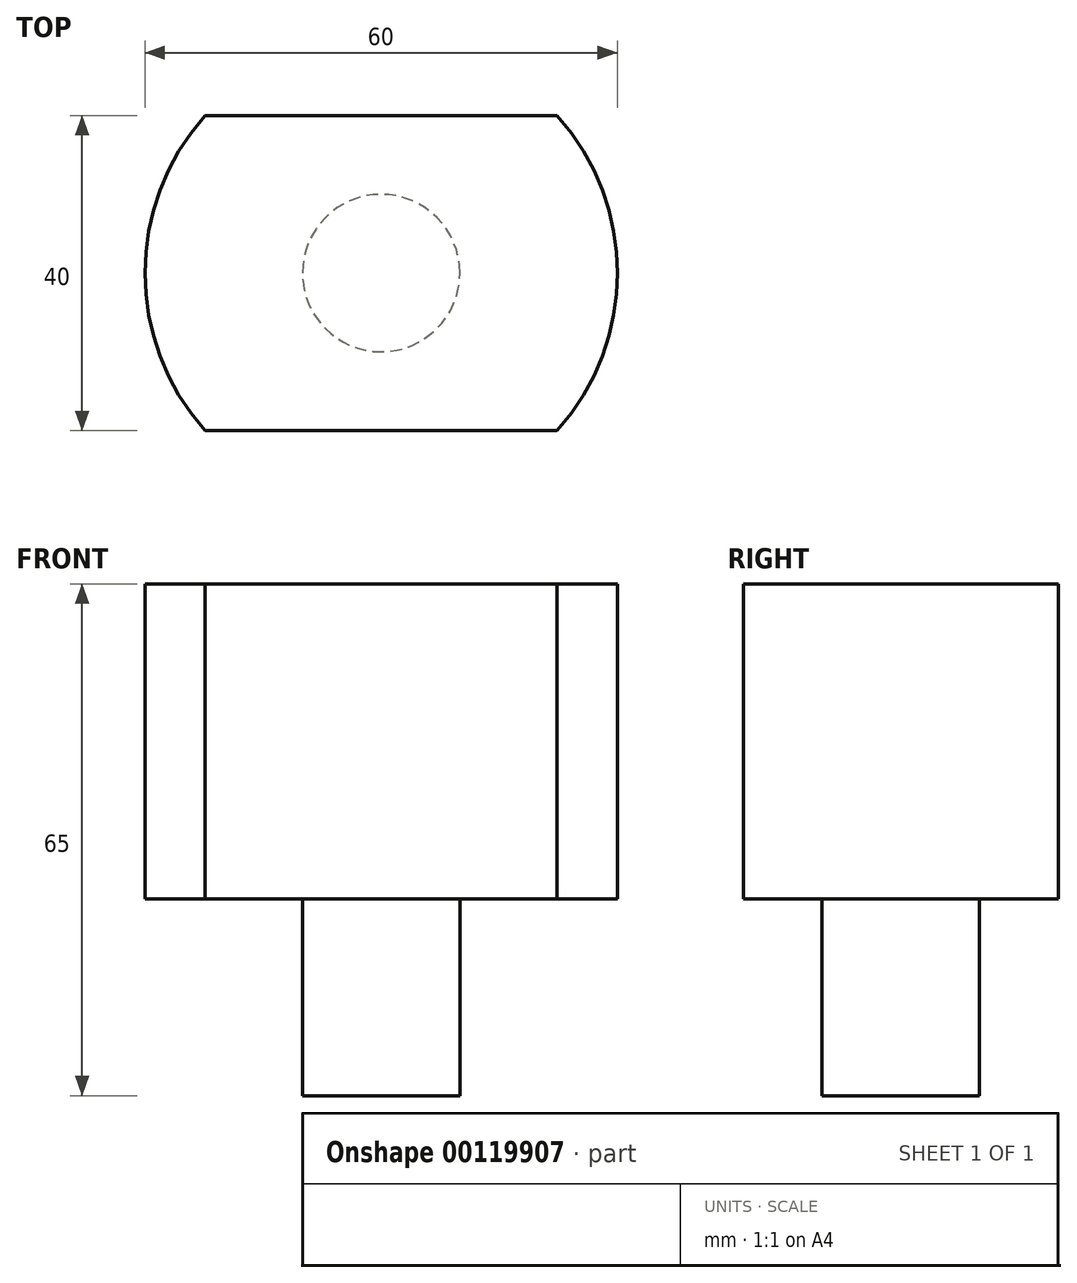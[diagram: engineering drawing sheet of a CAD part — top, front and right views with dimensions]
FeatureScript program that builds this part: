
annotation { "Feature Type Name" : "Feature", "Feature Type Description" : "" }
export const myFeature = defineFeature(function(context is Context, id is Id, definition is map)
    precondition{}
    {
        {
            var Q0;
            Q0=qCreatedBy(makeId("Top.planeOp"),FACE);
            var sketch = newSketch(context, id + "F0", { "sketchPlane" : qUnion([Q0])});
            skArc(sketch, "E0", {"start": v(-22.36, 20) * mm, "mid": v(-30, 0) * mm, "end": v(-22.36, -20) * mm});
            skLineSegment(sketch, "E1", {"start": v(-22.36, 20) * mm, "end": v(22.36, 20) * mm});
            skLineSegment(sketch, "E2", {"start": v(-22.36, -20) * mm, "end": v(22.36, -20) * mm});
            skArc(sketch, "E3.trimOffspring", {"start": v(22.36, -20) * mm, "mid": v(30, 0) * mm, "end": v(22.36, 20) * mm});
            skSolve(sketch);
        }
        {
            var Q0;
            Q0=makeQuery(id+"F0.imprint","IMPRINT",FACE,{"disambiguationData":[TD([[makeQuery(id+"F0.imprint","IMPRINT",EDGE,{"derivedFrom":sQuery(id+"F0.wireOp",EDGE,"E0")}),1.0]])]});
            extrude(context, id + "F1", {"entities" : qUnion([Q0]), "endBound" : BoundingType.SYMMETRIC, "depth" : 40 * mm});
        }
        {
            var Q0;
            Q0=makeQuery(id+"F1.opExtrude","CAP_FACE",FACE,{"disambiguationData":[OSD([sQuery(id+"F0.wireOp",EDGE,"E0"),sQuery(id+"F0.wireOp",EDGE,"E1"),sQuery(id+"F0.wireOp",EDGE,"E2"),sQuery(id+"F0.wireOp",EDGE,"E3.trimOffspring")])],"isStart":true});
            var sketch = newSketch(context, id + "F2", { "sketchPlane" : qUnion([Q0])});
            skCircle(sketch, "E4", {"center": v(0, 0) * mm, "radius": 10 * mm});
            skSolve(sketch);
        }
        {
            var Q0;
            Q0=makeQuery(id+"F2.imprint","IMPRINT",FACE,{"disambiguationData":[TD([[makeQuery(id+"F2.imprint","IMPRINT",EDGE,{"derivedFrom":sQuery(id+"F2.wireOp",EDGE,"E4")}),1.0]])]});
            extrude(context, id + "F3", {"entities" : qUnion([Q0]), "operationType" : NewBodyOperationType.ADD, "depth" : 25 * mm});
        }
    });
